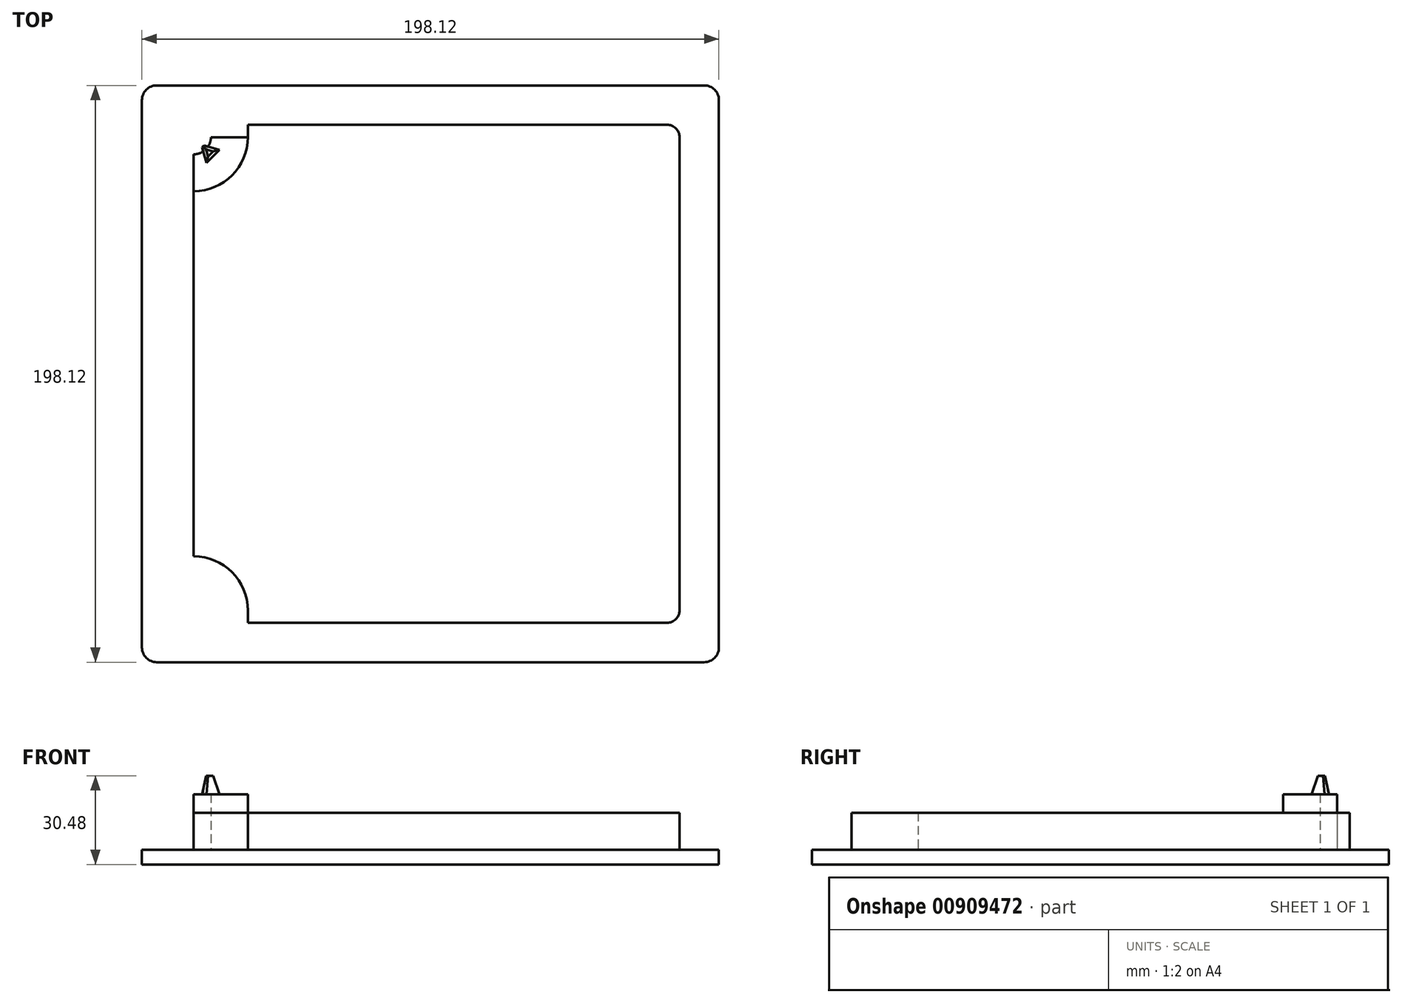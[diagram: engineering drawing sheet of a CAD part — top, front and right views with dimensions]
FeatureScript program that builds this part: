
annotation { "Feature Type Name" : "Feature", "Feature Type Description" : "" }
export const myFeature = defineFeature(function(context is Context, id is Id, definition is map)
    precondition{}
    {
        {
            var Q0;
            Q0=qCreatedBy(makeId("Top.planeOp"),FACE);
            var sketch = newSketch(context, id + "F0", { "sketchPlane" : qUnion([Q0])});
            skLineSegment(sketch, "E0", {"start": v(-99.06, 0) * mm, "end": v(-99.06, -93.98) * mm, "construction": true});
            skArc(sketch, "E1", {"start": v(-99.06, -93.98) * mm, "mid": v(-97.57, -97.57) * mm, "end": v(-93.98, -99.06) * mm, "construction": true});
            skLineSegment(sketch, "E2", {"start": v(99.06, 0) * mm, "end": v(99.06, -93.98) * mm, "construction": true});
            skArc(sketch, "E3", {"start": v(93.98, -99.06) * mm, "mid": v(97.57, -97.57) * mm, "end": v(99.06, -93.98) * mm, "construction": true});
            skLineSegment(sketch, "E4", {"start": v(93.98, -99.06) * mm, "end": v(-93.98, -99.06) * mm, "construction": true});
            skLineSegment(sketch, "E5", {"start": v(-99.06, 0) * mm, "end": v(99.06, 0) * mm, "construction": true});
            skLineSegment(sketch, "E6.0", {"start": v(-99.06, 0) * mm, "end": v(-99.06, -93.98) * mm});
            skLineSegment(sketch, "E6.1", {"start": v(99.06, 0) * mm, "end": v(99.06, -93.98) * mm});
            skArc(sketch, "E6.2", {"start": v(93.98, -99.06) * mm, "mid": v(97.57, -97.57) * mm, "end": v(99.06, -93.98) * mm});
            skLineSegment(sketch, "E6.3", {"start": v(-99.06, 0) * mm, "end": v(99.06, 0) * mm});
            skLineSegment(sketch, "E6.4", {"start": v(93.98, -99.06) * mm, "end": v(-93.98, -99.06) * mm});
            skArc(sketch, "E6.5", {"start": v(-99.06, -93.98) * mm, "mid": v(-97.57, -97.57) * mm, "end": v(-93.98, -99.06) * mm});
            skSolve(sketch);
        }
        {
            var Q0;
            Q0=qCreatedBy(makeId("Right.planeOp"),FACE);
            var sketch = newSketch(context, id + "F1", { "sketchPlane" : qUnion([Q0])});
            skLineSegment(sketch, "E7", {"start": v(0, 0) * mm, "end": v(0, 257.79) * mm});
            skSolve(sketch);
        }
        {
            var Q0;
            Q0=qSketchRegion(id+"F0",true);
            extrude(context, id + "F2", {"entities" : qUnion([Q0]), "depth" : 5.08 * mm, "offsetDistance" : 25.4 * mm});
        }
        {
            var Q0;
            Q0=makeQuery(id+"F2.opExtrude","SWEPT_BODY",BODY,{"disambiguationData":[OSD([sQuery(id+"F0.wireOp",EDGE,"E6.0"),sQuery(id+"F0.wireOp",EDGE,"E6.1"),sQuery(id+"F0.wireOp",EDGE,"E6.2"),sQuery(id+"F0.wireOp",EDGE,"E6.3"),sQuery(id+"F0.wireOp",EDGE,"E6.4"),sQuery(id+"F0.wireOp",EDGE,"E6.5")])]});
            var Q1;
            Q1=qCreatedBy(makeId("Front.planeOp"),FACE);
            mirror(context, id + "F3", {"operationType" : NewBodyOperationType.ADD, "entities" : qUnion([Q0]), "mirrorPlane" : qUnion([Q1])});
        }
        {
            var Q0;
            {var subQ0=makeQuery(id+"F2.opExtrude","CAP_FACE",FACE,{"disambiguationData":[OSD([sQuery(id+"F0.wireOp",EDGE,"E6.0"),sQuery(id+"F0.wireOp",EDGE,"E6.1"),sQuery(id+"F0.wireOp",EDGE,"E6.2"),sQuery(id+"F0.wireOp",EDGE,"E6.3"),sQuery(id+"F0.wireOp",EDGE,"E6.4"),sQuery(id+"F0.wireOp",EDGE,"E6.5")])],"isStart":false});Q0=makeQuery(id+"F3.boolean.opBoolean","MERGE",FACE,{"derivedFrom":[subQ0,makeQuery(id+"F3.opPattern","COPY",FACE,{"derivedFrom":subQ0,"instanceName":"1"})]});}
            var sketch = newSketch(context, id + "F4", { "sketchPlane" : qUnion([Q0])});
            skLineSegment(sketch, "E8.bottom", {"start": v(81.28, 86.36) * mm, "end": v(-81.28, 86.36) * mm});
            skLineSegment(sketch, "E8.top", {"start": v(81.28, -86.36) * mm, "end": v(-81.28, -86.36) * mm});
            skLineSegment(sketch, "E8.left", {"start": v(86.36, 81.28) * mm, "end": v(86.36, -81.28) * mm});
            skLineSegment(sketch, "E8.right", {"start": v(-86.36, 81.28) * mm, "end": v(-86.36, -81.28) * mm});
            skPoint(sketch, "E8.middle", {"position": v(0, 0) * mm});
            skPoint(sketch, "E9.visualSharp", {"position": v(-86.36, 86.36) * mm});
            skArc(sketch, "E9.filletArc", {"start": v(-81.28, 86.36) * mm, "mid": v(-84.87, 84.87) * mm, "end": v(-86.36, 81.28) * mm});
            skPoint(sketch, "E10.visualSharp", {"position": v(86.36, 86.36) * mm});
            skArc(sketch, "E10.filletArc", {"start": v(86.36, 81.28) * mm, "mid": v(84.87, 84.87) * mm, "end": v(81.28, 86.36) * mm});
            skPoint(sketch, "E11.visualSharp", {"position": v(86.36, -86.36) * mm});
            skArc(sketch, "E11.filletArc", {"start": v(81.28, -86.36) * mm, "mid": v(84.87, -84.87) * mm, "end": v(86.36, -81.28) * mm});
            skPoint(sketch, "E12.visualSharp", {"position": v(-86.36, -86.36) * mm});
            skArc(sketch, "E12.filletArc", {"start": v(-86.36, -81.28) * mm, "mid": v(-84.87, -84.87) * mm, "end": v(-81.28, -86.36) * mm});
            skSolve(sketch);
        }
        {
            var Q0;
            Q0=makeQuery(id+"F4.imprint","IMPRINT",FACE,{"disambiguationData":[TD([[makeQuery(id+"F4.imprint","IMPRINT",EDGE,{"derivedFrom":sQuery(id+"F4.wireOp",EDGE,"E8.bottom")}),-1.0]])]});
            var sketch = newSketch(context, id + "F5", { "sketchPlane" : qUnion([Q0])});
            skArc(sketch, "E13", {"start": v(-81.28, 76.2) * mm, "mid": v(-84.87, 74.71) * mm, "end": v(-86.36, 71.12) * mm, "construction": true});
            skArc(sketch, "E14", {"start": v(-81.28, 76.2) * mm, "mid": v(-77.69, 77.69) * mm, "end": v(-76.2, 81.28) * mm, "construction": true});
            skArc(sketch, "E15", {"start": v(-71.12, 86.36) * mm, "mid": v(-74.71, 84.87) * mm, "end": v(-76.2, 81.28) * mm, "construction": true});
            skSolve(sketch);
        }
        {
            var Q0;
            Q0=makeQuery(id+"F5.imprint","IMPRINT",FACE,{"disambiguationData":[TD([[makeQuery(id+"F5.imprint","IMPRINT",EDGE,{"derivedFrom":makeQuery(id+"F4.imprint","IMPRINT",EDGE,{"derivedFrom":sQuery(id+"F4.wireOp",EDGE,"E8.bottom")})}),1.0]])]});
            var sketch = newSketch(context, id + "F6", { "sketchPlane" : qUnion([Q0])});
            skArc(sketch, "E16", {"start": v(-81.28, 75.39) * mm, "mid": v(-77.11, 77.11) * mm, "end": v(-75.39, 81.28) * mm});
            skArc(sketch, "E17", {"start": v(-81.28, 62.69) * mm, "mid": v(-68.13, 68.13) * mm, "end": v(-62.69, 81.28) * mm});
            skLineSegment(sketch, "E18", {"start": v(-75.39, 81.28) * mm, "end": v(-62.69, 81.28) * mm});
            skLineSegment(sketch, "E19", {"start": v(-81.28, 75.39) * mm, "end": v(-81.28, 62.69) * mm});
            skSolve(sketch);
        }
        {
            var Q0;
            Q0 = qSketchRegion(id + "F6", true);
            var Q1;
            Q1=sQuery(id+"F6.wireOp",EDGE,"E18");
            var Q2;
            Q2 = qBodyType(qCreatedBy(id + "F6" ,EDGE), BodyType.WIRE);
            extrude(context, id + "F7", {"entities" : qUnion([Q0]), "operationType" : NewBodyOperationType.ADD, "surfaceEntities" : qUnion([Q1, Q2]), "depth" : 19.05 * mm, "offsetDistance" : 25.4 * mm});
        }
        {
            var Q0;
            Q0=makeQuery(id+"F5.imprint","IMPRINT",FACE,{"disambiguationData":[TD([[makeQuery(id+"F5.imprint","IMPRINT",EDGE,{"derivedFrom":makeQuery(id+"F4.imprint","IMPRINT",EDGE,{"derivedFrom":sQuery(id+"F4.wireOp",EDGE,"E8.bottom")})}),1.0]])]});
            var sketch = newSketch(context, id + "F8", { "sketchPlane" : qUnion([Q0])});
            skLineSegment(sketch, "E20", {"start": v(-62.69, 81.28) * mm, "end": v(-62.69, 85.55) * mm});
            skLineSegment(sketch, "E21", {"start": v(-62.69, 85.55) * mm, "end": v(81.28, 85.55) * mm});
            skArc(sketch, "E22", {"start": v(85.55, 81.28) * mm, "mid": v(84.3, 84.3) * mm, "end": v(81.28, 85.55) * mm});
            skLineSegment(sketch, "E23", {"start": v(85.55, 81.28) * mm, "end": v(85.55, -81.28) * mm});
            skArc(sketch, "E24", {"start": v(81.28, -85.55) * mm, "mid": v(84.3, -84.3) * mm, "end": v(85.55, -81.28) * mm});
            skLineSegment(sketch, "E25", {"start": v(81.28, -85.55) * mm, "end": v(-62.69, -85.55) * mm});
            skLineSegment(sketch, "E26", {"start": v(-62.69, -81.28) * mm, "end": v(-62.69, -85.55) * mm});
            skArc(sketch, "E27", {"start": v(-81.28, 62.69) * mm, "mid": v(-68.13, 68.13) * mm, "end": v(-62.69, 81.28) * mm});
            skArc(sketch, "E28", {"start": v(-62.69, -81.28) * mm, "mid": v(-68.13, -68.13) * mm, "end": v(-81.28, -62.69) * mm});
            skLineSegment(sketch, "E29", {"start": v(-81.28, -62.69) * mm, "end": v(-81.28, 62.69) * mm});
            skSolve(sketch);
        }
        {
            var Q0;
            Q0 = qSketchRegion(id + "F8", true);
            extrude(context, id + "F9", {"entities" : qUnion([Q0]), "operationType" : NewBodyOperationType.ADD, "depth" : 12.7 * mm, "offsetDistance" : 25.4 * mm});
        }
        {
            var Q0;
            Q0=makeQuery(id+"F7.opExtrude","CAP_FACE",FACE,{"disambiguationData":[OSD([sQuery(id+"F6.wireOp",EDGE,"E16"),sQuery(id+"F6.wireOp",EDGE,"E17"),sQuery(id+"F6.wireOp",EDGE,"E18"),sQuery(id+"F6.wireOp",EDGE,"E19")])],"isStart":false});
            var sketch = newSketch(context, id + "F10", { "sketchPlane" : qUnion([Q0])});
            skLineSegment(sketch, "E30", {"start": v(-76.94, 72.45) * mm, "end": v(-78.59, 78.59) * mm, "construction": true});
            skLineSegment(sketch, "E31", {"start": v(-78.59, 78.59) * mm, "end": v(-72.45, 76.94) * mm, "construction": true});
            skLineSegment(sketch, "E32", {"start": v(-72.45, 76.94) * mm, "end": v(-76.94, 72.45) * mm});
            skLineSegment(sketch, "E33", {"start": v(-81.28, 81.28) * mm, "end": v(-78.59, 78.59) * mm, "construction": true});
            skLineSegment(sketch, "E34", {"start": v(-77.8, 78.38) * mm, "end": v(-78.38, 77.8) * mm});
            skLineSegment(sketch, "E35", {"start": v(-77.8, 78.38) * mm, "end": v(-72.45, 76.94) * mm});
            skLineSegment(sketch, "E36", {"start": v(-78.38, 77.8) * mm, "end": v(-76.94, 72.45) * mm});
            skSolve(sketch);
        }
        {
            var Q0;
            Q0 = qSketchRegion(id + "F10", true);
            extrude(context, id + "F11", {"entities" : qUnion([Q0]), "operationType" : NewBodyOperationType.ADD, "depth" : 6.35 * mm, "offsetDistance" : 25.4 * mm, "hasDraft" : true, "draftAngle" : 10 * degree, "draftPullDirection" : true});
        }
    });
